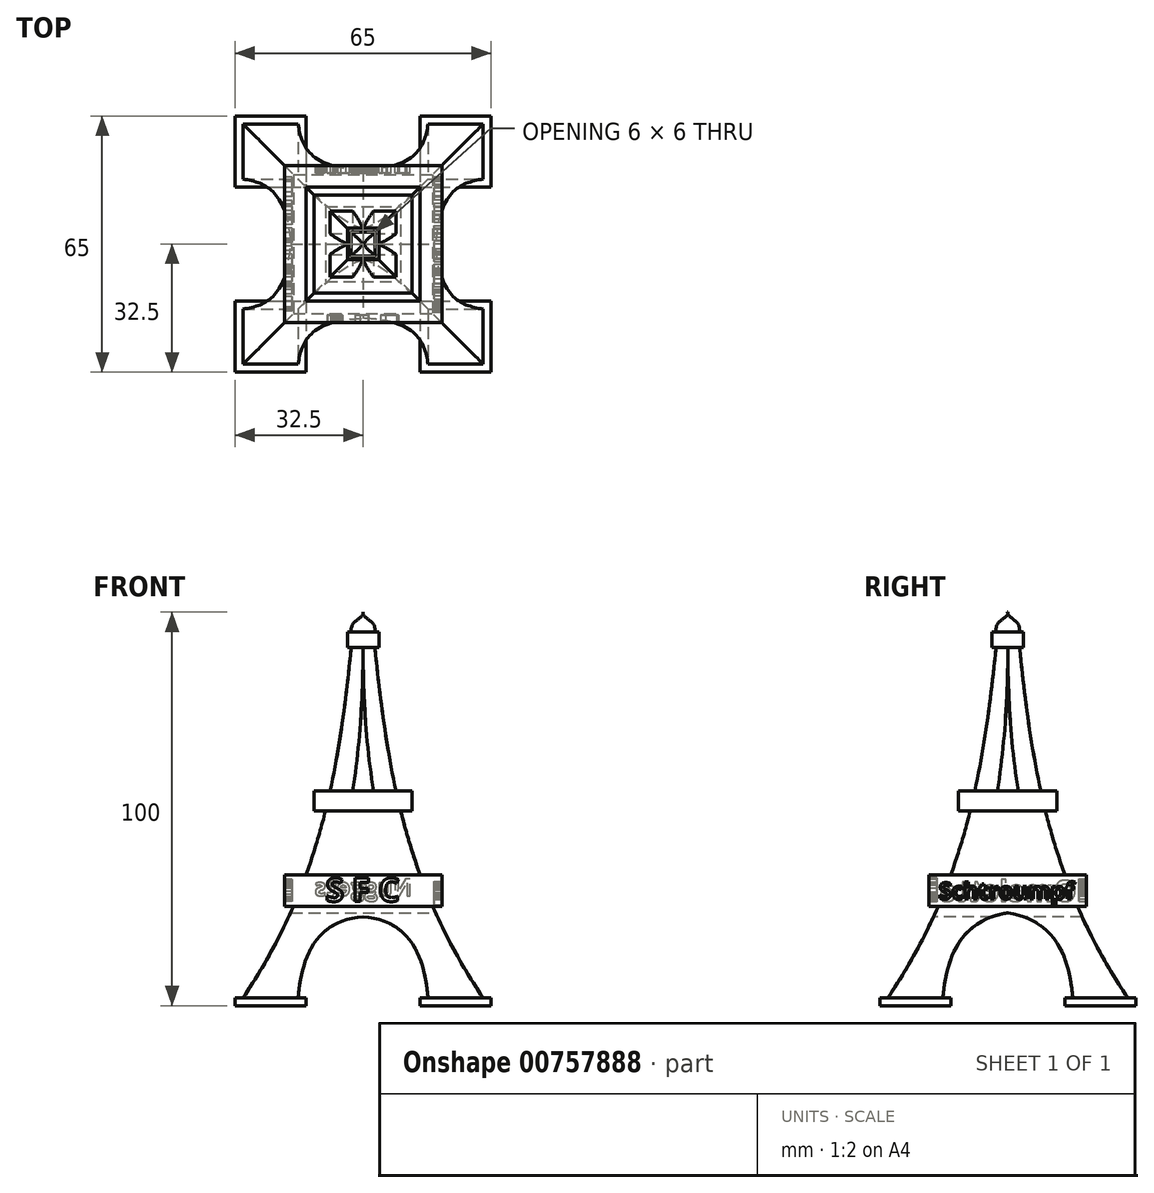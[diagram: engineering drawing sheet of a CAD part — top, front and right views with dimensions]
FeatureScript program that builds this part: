
annotation { "Feature Type Name" : "Feature", "Feature Type Description" : "" }
export const myFeature = defineFeature(function(context is Context, id is Id, definition is map)
    precondition{}
    {
        {
            var Q0;
            Q0=qCreatedBy(makeId("Front.planeOp"),FACE);
            var sketch = newSketch(context, id + "F0", { "sketchPlane" : qUnion([Q0])});
            skLineSegment(sketch, "E0.bottom", {"start": v(-32.5, 53.76) * mm, "end": v(32.5, 53.76) * mm});
            skLineSegment(sketch, "E0.top", {"start": v(-32.5, -46.24) * mm, "end": v(32.5, -46.24) * mm});
            skLineSegment(sketch, "E0.left", {"start": v(-32.5, 53.76) * mm, "end": v(-32.5, -46.24) * mm});
            skLineSegment(sketch, "E0.right", {"start": v(32.5, 53.76) * mm, "end": v(32.5, -46.24) * mm});
            skSolve(sketch);
        }
        {
            var Q0;
            Q0=makeQuery(id+"F0.imprint","IMPRINT",FACE,{"disambiguationData":[TD([[makeQuery(id+"F0.imprint","IMPRINT",EDGE,{"derivedFrom":sQuery(id+"F0.wireOp",EDGE,"E0.bottom")}),-1.0]])]});
            extrude(context, id + "F1", {"entities" : qUnion([Q0]), "endBound" : BoundingType.SYMMETRIC, "depth" : 65 * mm, "offsetDistance" : 25 * mm});
        }
        {
            var Q0;
            Q0=makeQuery(id+"F1.opExtrude","CAP_FACE",FACE,{"disambiguationData":[OSD([sQuery(id+"F0.wireOp",EDGE,"E0.bottom"),sQuery(id+"F0.wireOp",EDGE,"E0.top"),sQuery(id+"F0.wireOp",EDGE,"E0.left"),sQuery(id+"F0.wireOp",EDGE,"E0.right")])],"isStart":false});
            var sketch = newSketch(context, id + "F2", { "sketchPlane" : qUnion([Q0])});
            skLineSegment(sketch, "E1", {"start": v(0, 61.54) * mm, "end": v(0, -56.46) * mm, "construction": true});
            skLineSegment(sketch, "E2.bottom", {"start": v(-4, 48.76) * mm, "end": v(-3, 48.76) * mm});
            skLineSegment(sketch, "E2.top", {"start": v(-4, 44.76) * mm, "end": v(-3, 44.76) * mm});
            skLineSegment(sketch, "E2.left", {"start": v(-4, 48.76) * mm, "end": v(-4, 44.76) * mm});
            skLineSegment(sketch, "E2.right", {"start": v(4, 48.76) * mm, "end": v(4, 44.76) * mm});
            skLineSegment(sketch, "E3.bottom", {"start": v(-32.5, -44.24) * mm, "end": v(-30.5, -44.24) * mm});
            skLineSegment(sketch, "E3.top", {"start": v(-32.5, -46.24) * mm, "end": v(-14.5, -46.24) * mm});
            skLineSegment(sketch, "E3.left", {"start": v(-32.5, -44.24) * mm, "end": v(-32.5, -46.24) * mm});
            skLineSegment(sketch, "E3.right", {"start": v(-14.5, -44.24) * mm, "end": v(-14.5, -46.24) * mm});
            skLineSegment(sketch, "E4.bottom", {"start": v(14.5, -44.24) * mm, "end": v(16.5, -44.24) * mm});
            skLineSegment(sketch, "E4.top", {"start": v(14.5, -46.24) * mm, "end": v(32.5, -46.24) * mm});
            skLineSegment(sketch, "E4.left", {"start": v(14.5, -44.24) * mm, "end": v(14.5, -46.24) * mm});
            skLineSegment(sketch, "E4.right", {"start": v(32.5, -44.24) * mm, "end": v(32.5, -46.24) * mm});
            skFitSpline(sketch, "E5", {"points": [v(-30.5, -44.24) * mm, v(-3, 44.76) * mm], "startDerivative": vector(57.75, 85.5) * mm, "endDerivative": vector(9.94, 98.57) * mm});
            skFitSpline(sketch, "E6.MirrorCS", {"points": [v(30.5, -44.24) * mm, v(3, 44.76) * mm], "startDerivative": vector(-57.75, 85.5) * mm, "endDerivative": vector(-9.94, 98.57) * mm});
            skLineSegment(sketch, "E7.bottom", {"start": v(-20, -12.96) * mm, "end": v(-14.48, -12.96) * mm});
            skLineSegment(sketch, "E7.top", {"start": v(-20, -20.96) * mm, "end": v(-17.68, -20.96) * mm});
            skLineSegment(sketch, "E7.left", {"start": v(-20, -12.96) * mm, "end": v(-20, -20.96) * mm});
            skLineSegment(sketch, "E7.right", {"start": v(20, -12.96) * mm, "end": v(20, -20.96) * mm});
            skLineSegment(sketch, "E8.bottom", {"start": v(-12.5, 8.3) * mm, "end": v(-8.38, 8.3) * mm});
            skLineSegment(sketch, "E8.top", {"start": v(-12.5, 3.3) * mm, "end": v(-9.55, 3.3) * mm});
            skLineSegment(sketch, "E8.left", {"start": v(-12.5, 8.3) * mm, "end": v(-12.5, 3.3) * mm});
            skLineSegment(sketch, "E8.right", {"start": v(12.5, 8.3) * mm, "end": v(12.5, 3.3) * mm});
            skFitSpline(sketch, "E9", {"points": [v(0, 44.76) * mm, v(-7, -12.96) * mm], "startDerivative": vector(0, -64.38) * mm, "endDerivative": vector(-14.24, -56.15) * mm});
            skFitSpline(sketch, "E10.MirrorCS", {"points": [v(0, 44.76) * mm, v(7, -12.96) * mm], "startDerivative": vector(0, -64.38) * mm, "endDerivative": vector(14.24, -56.15) * mm});
            skFitSpline(sketch, "E11", {"points": [v(0, 53.76) * mm, v(-3, 48.76) * mm], "startDerivative": vector(0, -6.46) * mm, "endDerivative": vector(0.9, -9.92) * mm});
            skFitSpline(sketch, "E12.MirrorCS", {"points": [v(0, 53.76) * mm, v(3, 48.76) * mm], "startDerivative": vector(0, -6.46) * mm, "endDerivative": vector(-0.9, -9.92) * mm});
            skLineSegment(sketch, "E13.trimOffspring", {"start": v(-16.5, -44.24) * mm, "end": v(-14.5, -44.24) * mm});
            skFitSpline(sketch, "E14", {"points": [v(-16.5, -44.24) * mm, v(0, -23.64) * mm], "startDerivative": vector(2.25, 24) * mm, "endDerivative": vector(40.5, 3.3) * mm});
            skFitSpline(sketch, "E15.MirrorCS", {"points": [v(16.5, -44.24) * mm, v(0, -23.64) * mm], "startDerivative": vector(-2.25, 24) * mm, "endDerivative": vector(-40.5, 3.3) * mm});
            skLineSegment(sketch, "E16.trimOffspring", {"start": v(30.5, -44.24) * mm, "end": v(32.5, -44.24) * mm});
            skFitSpline(sketch, "E17.trimOffspring", {"points": [v(-30.5, -44.24) * mm, v(-3, 44.76) * mm], "startDerivative": vector(57.75, 85.5) * mm, "endDerivative": vector(9.94, 98.57) * mm});
            skFitSpline(sketch, "E18.trimOffspring", {"points": [v(0, 44.76) * mm, v(-7, -12.96) * mm], "startDerivative": vector(0, -64.38) * mm, "endDerivative": vector(-14.24, -56.15) * mm});
            skFitSpline(sketch, "E19.trimOffspring", {"points": [v(-30.5, -44.24) * mm, v(-3, 44.76) * mm], "startDerivative": vector(57.75, 85.5) * mm, "endDerivative": vector(9.94, 98.57) * mm});
            skLineSegment(sketch, "E20.trimOffspring", {"start": v(8.38, 8.3) * mm, "end": v(12.5, 8.3) * mm});
            skLineSegment(sketch, "E21.trimOffspring", {"start": v(9.55, 3.3) * mm, "end": v(12.5, 3.3) * mm});
            skLineSegment(sketch, "E22.trimOffspring", {"start": v(-2.63, 8.3) * mm, "end": v(2.63, 8.3) * mm});
            skLineSegment(sketch, "E23.trimOffspring", {"start": v(-3.47, 3.3) * mm, "end": v(3.47, 3.3) * mm});
            skLineSegment(sketch, "E24.trimOffspring", {"start": v(14.48, -12.96) * mm, "end": v(20, -12.96) * mm});
            skLineSegment(sketch, "E25.trimOffspring", {"start": v(-7, -12.96) * mm, "end": v(7, -12.96) * mm});
            skLineSegment(sketch, "E26.trimOffspring", {"start": v(17.68, -20.96) * mm, "end": v(20, -20.96) * mm});
            skLineSegment(sketch, "E27.trimOffspring", {"start": v(3, 44.76) * mm, "end": v(4, 44.76) * mm});
            skLineSegment(sketch, "E28.trimOffspring", {"start": v(3, 48.76) * mm, "end": v(4, 48.76) * mm});
            skFitSpline(sketch, "E29.trimOffspring", {"points": [v(30.5, -44.24) * mm, v(3, 44.76) * mm], "startDerivative": vector(-57.75, 85.5) * mm, "endDerivative": vector(-9.94, 98.57) * mm});
            skSolve(sketch);
        }
        {
            var Q0;
            Q0=makeQuery(id+"F2.imprint","IMPRINT",FACE,{"disambiguationData":[TD([[makeQuery(id+"F2.imprint","IMPRINT",EDGE,{"derivedFrom":sQuery(id+"F2.wireOp",EDGE,"E2.bottom")}),1.0]])]});
            var Q1;
            Q1=makeQuery(id+"F2.imprint","IMPRINT",FACE,{"disambiguationData":[TD([[makeQuery(id+"F2.imprint","IMPRINT",EDGE,{"derivedFrom":sQuery(id+"F2.wireOp",EDGE,"E2.right")}),1.0]])]});
            var Q2;
            {var subQ0=sQuery(id+"F2.wireOp",EDGE,"E9");Q2=makeQuery(id+"F2.imprint","IMPRINT",FACE,{"disambiguationData":[TD([[makeQuery(id+"F2.imprint","IMPRINT",EDGE,{"derivedFrom":subQ0}),1.0]])]});}
            var Q3;
            Q3=makeQuery(id+"F2.imprint","IMPRINT",FACE,{"disambiguationData":[TD([[makeQuery(id+"F2.imprint","IMPRINT",EDGE,{"derivedFrom":sQuery(id+"F2.wireOp",EDGE,"E18.trimOffspring")}),1.0]])]});
            var Q4;
            {var subQ1=sQuery(id+"F2.wireOp",EDGE,"E3.right");Q4=makeQuery(id+"F2.imprint","IMPRINT",FACE,{"disambiguationData":[TD([[makeQuery(id+"F2.imprint","IMPRINT",EDGE,{"derivedFrom":subQ1}),1.0]])]});}
            extrude(context, id + "F3", {"entities" : qUnion([Q0, Q1, Q2, Q3, Q4]), "operationType" : NewBodyOperationType.REMOVE, "oppositeDirection" : true, "depth" : 70 * mm, "offsetDistance" : 25 * mm});
        }
        {
            var Q0;
            Q0=qCreatedBy(makeId("Right.planeOp"),FACE);
            var sketch = newSketch(context, id + "F4", { "sketchPlane" : qUnion([Q0])});
            skLineSegment(sketch, "E30", {"start": v(0, 66.27) * mm, "end": v(0, -51.73) * mm, "construction": true});
            skLineSegment(sketch, "E31.bottom", {"start": v(-4, 48.76) * mm, "end": v(-3, 48.76) * mm});
            skLineSegment(sketch, "E31.top", {"start": v(-4, 44.76) * mm, "end": v(-3, 44.76) * mm});
            skLineSegment(sketch, "E31.left", {"start": v(-4, 48.76) * mm, "end": v(-4, 44.76) * mm});
            skLineSegment(sketch, "E31.right", {"start": v(4, 48.76) * mm, "end": v(4, 44.76) * mm});
            skLineSegment(sketch, "E32.bottom", {"start": v(-32.5, -44.24) * mm, "end": v(-30.5, -44.24) * mm});
            skLineSegment(sketch, "E32.top", {"start": v(-32.5, -46.24) * mm, "end": v(-14.5, -46.24) * mm});
            skLineSegment(sketch, "E32.left", {"start": v(-32.5, -44.24) * mm, "end": v(-32.5, -46.24) * mm});
            skLineSegment(sketch, "E32.right", {"start": v(-14.5, -44.24) * mm, "end": v(-14.5, -46.24) * mm});
            skLineSegment(sketch, "E33.bottom", {"start": v(14.5, -44.24) * mm, "end": v(16.5, -44.24) * mm});
            skLineSegment(sketch, "E33.top", {"start": v(14.5, -46.24) * mm, "end": v(32.5, -46.24) * mm});
            skLineSegment(sketch, "E33.left", {"start": v(14.5, -44.24) * mm, "end": v(14.5, -46.24) * mm});
            skLineSegment(sketch, "E33.right", {"start": v(32.5, -44.24) * mm, "end": v(32.5, -46.24) * mm});
            skFitSpline(sketch, "E34", {"points": [v(-30.5, -44.24) * mm, v(-3, 44.76) * mm], "startDerivative": vector(57.75, 85.5) * mm, "endDerivative": vector(9.94, 98.57) * mm});
            skFitSpline(sketch, "E35.MirrorCS", {"points": [v(30.5, -44.24) * mm, v(3, 44.76) * mm], "startDerivative": vector(-57.75, 85.5) * mm, "endDerivative": vector(-9.94, 98.57) * mm});
            skLineSegment(sketch, "E36.bottom", {"start": v(-20, -12.96) * mm, "end": v(-14.48, -12.96) * mm});
            skLineSegment(sketch, "E36.top", {"start": v(-20, -20.96) * mm, "end": v(-17.68, -20.96) * mm});
            skLineSegment(sketch, "E36.left", {"start": v(-20, -12.96) * mm, "end": v(-20, -20.96) * mm});
            skLineSegment(sketch, "E36.right", {"start": v(20, -12.96) * mm, "end": v(20, -20.96) * mm});
            skLineSegment(sketch, "E37.bottom", {"start": v(-12.5, 8.3) * mm, "end": v(-8.38, 8.3) * mm});
            skLineSegment(sketch, "E37.top", {"start": v(-12.5, 3.3) * mm, "end": v(-9.55, 3.3) * mm});
            skLineSegment(sketch, "E37.left", {"start": v(-12.5, 8.3) * mm, "end": v(-12.5, 3.3) * mm});
            skLineSegment(sketch, "E37.right", {"start": v(12.5, 8.3) * mm, "end": v(12.5, 3.3) * mm});
            skFitSpline(sketch, "E38", {"points": [v(0, 44.76) * mm, v(-7, -12.96) * mm], "startDerivative": vector(0, -64.38) * mm, "endDerivative": vector(-14.24, -56.15) * mm});
            skFitSpline(sketch, "E39.MirrorCS", {"points": [v(0, 44.76) * mm, v(7, -12.96) * mm], "startDerivative": vector(0, -64.38) * mm, "endDerivative": vector(14.24, -56.15) * mm});
            skFitSpline(sketch, "E40", {"points": [v(0.08, 53.76) * mm, v(-3, 48.76) * mm], "startDerivative": vector(-0.24, -5.86) * mm, "endDerivative": vector(0.9, -9.92) * mm});
            skFitSpline(sketch, "E41.MirrorCS", {"points": [v(-0.08, 53.76) * mm, v(3, 48.76) * mm], "startDerivative": vector(0.24, -5.86) * mm, "endDerivative": vector(-0.9, -9.92) * mm});
            skLineSegment(sketch, "E42.trimOffspring", {"start": v(-16.5, -44.24) * mm, "end": v(-14.5, -44.24) * mm});
            skFitSpline(sketch, "E43", {"points": [v(-16.5, -44.24) * mm, v(0, -22.65) * mm], "startDerivative": vector(2.25, 24) * mm, "endDerivative": vector(40.5, 6.27) * mm});
            skFitSpline(sketch, "E44.MirrorCS", {"points": [v(16.5, -44.24) * mm, v(0, -22.65) * mm], "startDerivative": vector(-2.25, 24) * mm, "endDerivative": vector(-40.5, 6.27) * mm});
            skLineSegment(sketch, "E45.trimOffspring", {"start": v(30.5, -44.24) * mm, "end": v(32.5, -44.24) * mm});
            skFitSpline(sketch, "E46.trimOffspring", {"points": [v(30.5, -44.24) * mm, v(3, 44.76) * mm], "startDerivative": vector(-57.75, 85.5) * mm, "endDerivative": vector(-9.94, 98.57) * mm});
            skFitSpline(sketch, "E47.trimOffspring", {"points": [v(0, 44.76) * mm, v(-7, -12.96) * mm], "startDerivative": vector(0, -64.38) * mm, "endDerivative": vector(-14.24, -56.15) * mm});
            skFitSpline(sketch, "E48.trimOffspring", {"points": [v(0, 44.76) * mm, v(7, -12.96) * mm], "startDerivative": vector(0, -64.38) * mm, "endDerivative": vector(14.24, -56.15) * mm});
            skFitSpline(sketch, "E49.trimOffspring", {"points": [v(-30.5, -44.24) * mm, v(-3, 44.76) * mm], "startDerivative": vector(57.75, 85.5) * mm, "endDerivative": vector(9.94, 98.57) * mm});
            skLineSegment(sketch, "E50.trimOffspring", {"start": v(8.38, 8.3) * mm, "end": v(12.5, 8.3) * mm});
            skLineSegment(sketch, "E51.trimOffspring", {"start": v(9.55, 3.3) * mm, "end": v(12.5, 3.3) * mm});
            skLineSegment(sketch, "E52.trimOffspring", {"start": v(-2.63, 8.3) * mm, "end": v(2.63, 8.3) * mm});
            skLineSegment(sketch, "E53.trimOffspring", {"start": v(-3.47, 3.3) * mm, "end": v(3.47, 3.3) * mm});
            skLineSegment(sketch, "E54.trimOffspring", {"start": v(14.48, -12.96) * mm, "end": v(20, -12.96) * mm});
            skLineSegment(sketch, "E55.trimOffspring", {"start": v(-7, -12.96) * mm, "end": v(7, -12.96) * mm});
            skLineSegment(sketch, "E56.trimOffspring", {"start": v(17.68, -20.96) * mm, "end": v(20, -20.96) * mm});
            skLineSegment(sketch, "E57.trimOffspring", {"start": v(3, 44.76) * mm, "end": v(4, 44.76) * mm});
            skLineSegment(sketch, "E58.trimOffspring", {"start": v(3, 48.76) * mm, "end": v(4, 48.76) * mm});
            skFitSpline(sketch, "E59.trimOffspring", {"points": [v(30.5, -44.24) * mm, v(3, 44.76) * mm], "startDerivative": vector(-57.75, 85.5) * mm, "endDerivative": vector(-9.94, 98.57) * mm});
            skLineSegment(sketch, "E60.bottom", {"start": v(-32.5, -46.24) * mm, "end": v(32.5, -46.24) * mm});
            skLineSegment(sketch, "E60.top", {"start": v(-32.5, 53.76) * mm, "end": v(32.5, 53.76) * mm});
            skLineSegment(sketch, "E60.left", {"start": v(-32.5, -46.24) * mm, "end": v(-32.5, 53.76) * mm});
            skLineSegment(sketch, "E60.right", {"start": v(32.5, -46.24) * mm, "end": v(32.5, 53.76) * mm});
            skSolve(sketch);
        }
        {
            var Q0;
            Q0=makeQuery(id+"F4.imprint","IMPRINT",FACE,{"disambiguationData":[TD([[makeQuery(id+"F4.imprint","IMPRINT",EDGE,{"derivedFrom":sQuery(id+"F4.wireOp",EDGE,"E31.right")}),1.0]])]});
            var Q1;
            {var subQ0=sQuery(id+"F4.wireOp",EDGE,"E31.bottom");Q1=makeQuery(id+"F4.imprint","IMPRINT",FACE,{"disambiguationData":[TD([[makeQuery(id+"F4.imprint","IMPRINT",EDGE,{"derivedFrom":subQ0}),1.0]])]});}
            var Q2;
            {var subQ0=sQuery(id+"F4.wireOp",EDGE,"E38");Q2=makeQuery(id+"F4.imprint","IMPRINT",FACE,{"disambiguationData":[TD([[makeQuery(id+"F4.imprint","IMPRINT",EDGE,{"derivedFrom":subQ0}),1.0]])]});}
            var Q3;
            Q3=makeQuery(id+"F4.imprint","IMPRINT",FACE,{"disambiguationData":[TD([[makeQuery(id+"F4.imprint","IMPRINT",EDGE,{"derivedFrom":sQuery(id+"F4.wireOp",EDGE,"E47.trimOffspring")}),1.0]])]});
            var Q4;
            {var subQ1=sQuery(id+"F4.wireOp",EDGE,"E32.right");Q4=makeQuery(id+"F4.imprint","IMPRINT",FACE,{"disambiguationData":[TD([[makeQuery(id+"F4.imprint","IMPRINT",EDGE,{"derivedFrom":subQ1}),1.0]])]});}
            extrude(context, id + "F5", {"entities" : qUnion([Q0, Q1, Q2, Q3, Q4]), "operationType" : NewBodyOperationType.REMOVE, "endBound" : BoundingType.SYMMETRIC, "oppositeDirection" : true, "depth" : 70 * mm, "offsetDistance" : 25 * mm});
        }
        {
            var Q0;
            Q0=makeQuery(id+"F3.boolean.opBoolean","COPY",FACE,{"derivedFrom":makeQuery(id+"F3.opExtrude","SWEPT_FACE",FACE,{"disambiguationData":[OSD([sQuery(id+"F2.wireOp",EDGE,"E7.right")])]})});
            var sketch = newSketch(context, id + "F6", { "sketchPlane" : qUnion([Q0])});
            skText(sketch, "E61", { "text": "Schtroumpf", "fontName": "OpenSans-Bold.ttf"});
            const initialGuessF6  = {"E61": [-0.0175, -0.01917, 1, 0, 0.0042]};
            skSetInitialGuess(sketch, initialGuessF6);
            skSolve(sketch);
        }
        {
            var Q0;
            Q0 = qSketchRegion(id + "F6", true);
            extrude(context, id + "F7", {"entities" : qUnion([Q0]), "operationType" : NewBodyOperationType.REMOVE, "oppositeDirection" : true, "depth" : 2 * mm, "offsetDistance" : 25 * mm});
        }
        {
            var Q0;
            Q0=makeQuery(id+"F5.boolean.opBoolean","COPY",FACE,{"derivedFrom":makeQuery(id+"F5.opExtrude","SWEPT_FACE",FACE,{"disambiguationData":[OSD([sQuery(id+"F4.wireOp",EDGE,"E36.right")])]})});
            var sketch = newSketch(context, id + "F8", { "sketchPlane" : qUnion([Q0])});
            skText(sketch, "E62", { "text": "Nuggets", "fontName": "OpenSans-Bold.ttf"});
            const initialGuessF8  = {"E62": [-0.0125, -0.0183, 1, 0, 0.00434]};
            skSetInitialGuess(sketch, initialGuessF8);
            skSolve(sketch);
        }
        {
            var Q0;
            Q0 = qSketchRegion(id + "F8", true);
            extrude(context, id + "F9", {"entities" : qUnion([Q0]), "operationType" : NewBodyOperationType.REMOVE, "oppositeDirection" : true, "depth" : 2 * mm, "offsetDistance" : 25 * mm});
        }
        {
            var Q0;
            Q0=makeQuery(id+"F3.boolean.opBoolean","COPY",FACE,{"derivedFrom":makeQuery(id+"F3.opExtrude","SWEPT_FACE",FACE,{"disambiguationData":[OSD([sQuery(id+"F2.wireOp",EDGE,"E7.left")])]})});
            var sketch = newSketch(context, id + "F10", { "sketchPlane" : qUnion([Q0])});
            skText(sketch, "E63", { "text": "Omelette", "fontName": "OpenSans-Bold.ttf"});
            const initialGuessF10  = {"E63": [-0.0175, -0.0197, 1, 0, 0.00531]};
            skSetInitialGuess(sketch, initialGuessF10);
            skSolve(sketch);
        }
        {
            var Q0;
            Q0 = qSketchRegion(id + "F10", true);
            extrude(context, id + "F11", {"entities" : qUnion([Q0]), "operationType" : NewBodyOperationType.REMOVE, "oppositeDirection" : true, "depth" : 2 * mm, "offsetDistance" : 25 * mm});
        }
        {
            var Q0;
            Q0=makeQuery(id+"F5.boolean.opBoolean","COPY",FACE,{"derivedFrom":makeQuery(id+"F5.opExtrude","SWEPT_FACE",FACE,{"disambiguationData":[OSD([sQuery(id+"F4.wireOp",EDGE,"E36.left")])]})});
            var sketch = newSketch(context, id + "F12", { "sketchPlane" : qUnion([Q0])});
            skText(sketch, "E64", { "text": "S F C", "fontName": "OpenSans-Bold.ttf"});
            const initialGuessF12  = {"E64": [-0.0095, -0.01976, 1, 0, 0.00598]};
            skSetInitialGuess(sketch, initialGuessF12);
            skSolve(sketch);
        }
        {
            var Q0;
            Q0 = qSketchRegion(id + "F12", true);
            extrude(context, id + "F13", {"entities" : qUnion([Q0]), "operationType" : NewBodyOperationType.REMOVE, "oppositeDirection" : true, "depth" : 2 * mm, "offsetDistance" : 25 * mm});
        }
    });
